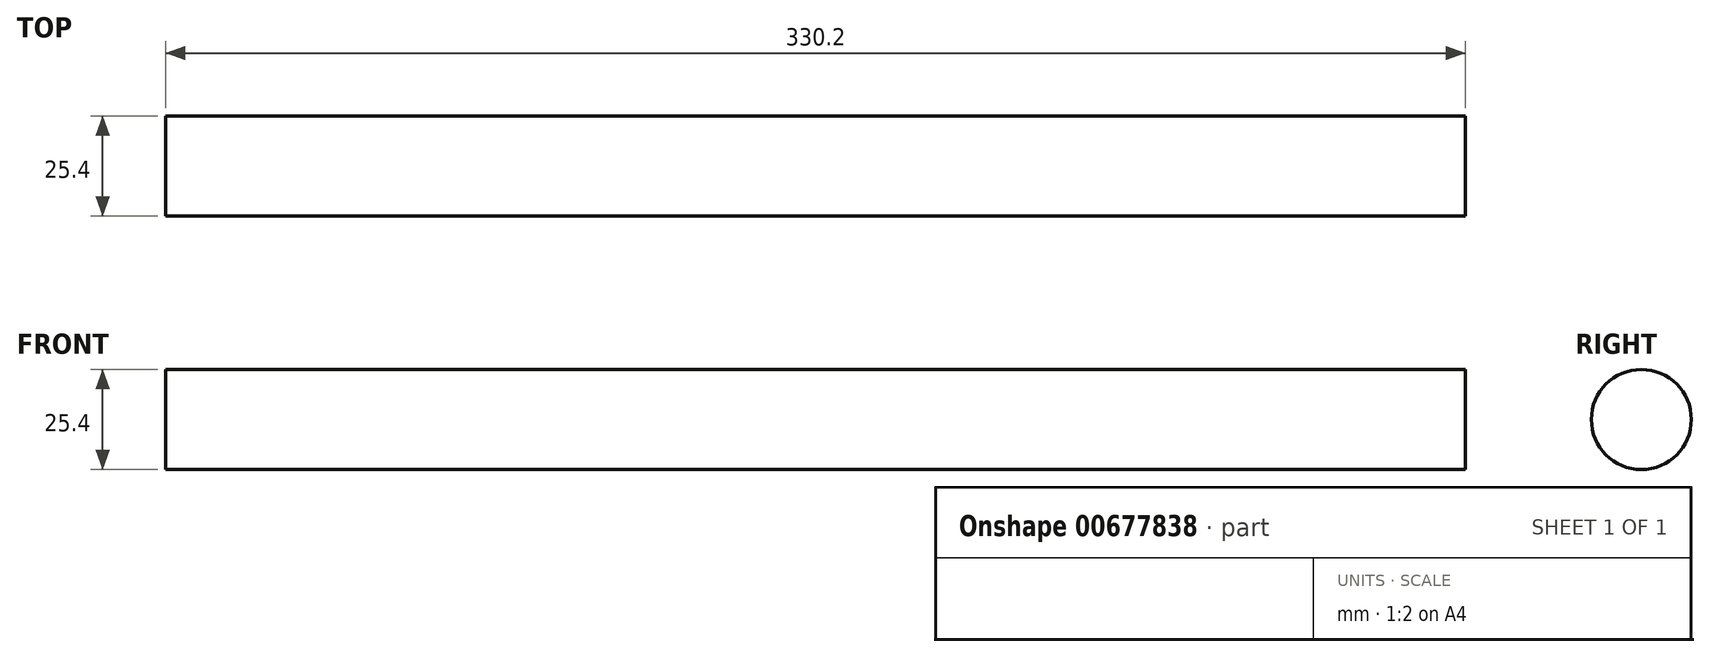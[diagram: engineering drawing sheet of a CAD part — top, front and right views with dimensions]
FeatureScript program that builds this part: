
annotation { "Feature Type Name" : "Feature", "Feature Type Description" : "" }
export const myFeature = defineFeature(function(context is Context, id is Id, definition is map)
    precondition{}
    {
        {
            var Q0;
            Q0=qCreatedBy(makeId("Right.planeOp"),FACE);
            var sketch = newSketch(context, id + "F0", { "sketchPlane" : qUnion([Q0])});
            skCircle(sketch, "E0", {"center": v(0, 0) * mm, "radius": 12.7 * mm});
            skSolve(sketch);
        }
        {
            var Q0;
            Q0=makeQuery(id+"F0.imprint","IMPRINT",FACE,{"disambiguationData":[TD([[makeQuery(id+"F0.imprint","IMPRINT",EDGE,{"derivedFrom":sQuery(id+"F0.wireOp",EDGE,"E0")}),1.0]])]});
            extrude(context, id + "F1", {"entities" : qUnion([Q0]), "depth" : 330.2 * mm, "offsetDistance" : 25.4 * mm});
        }
    });
